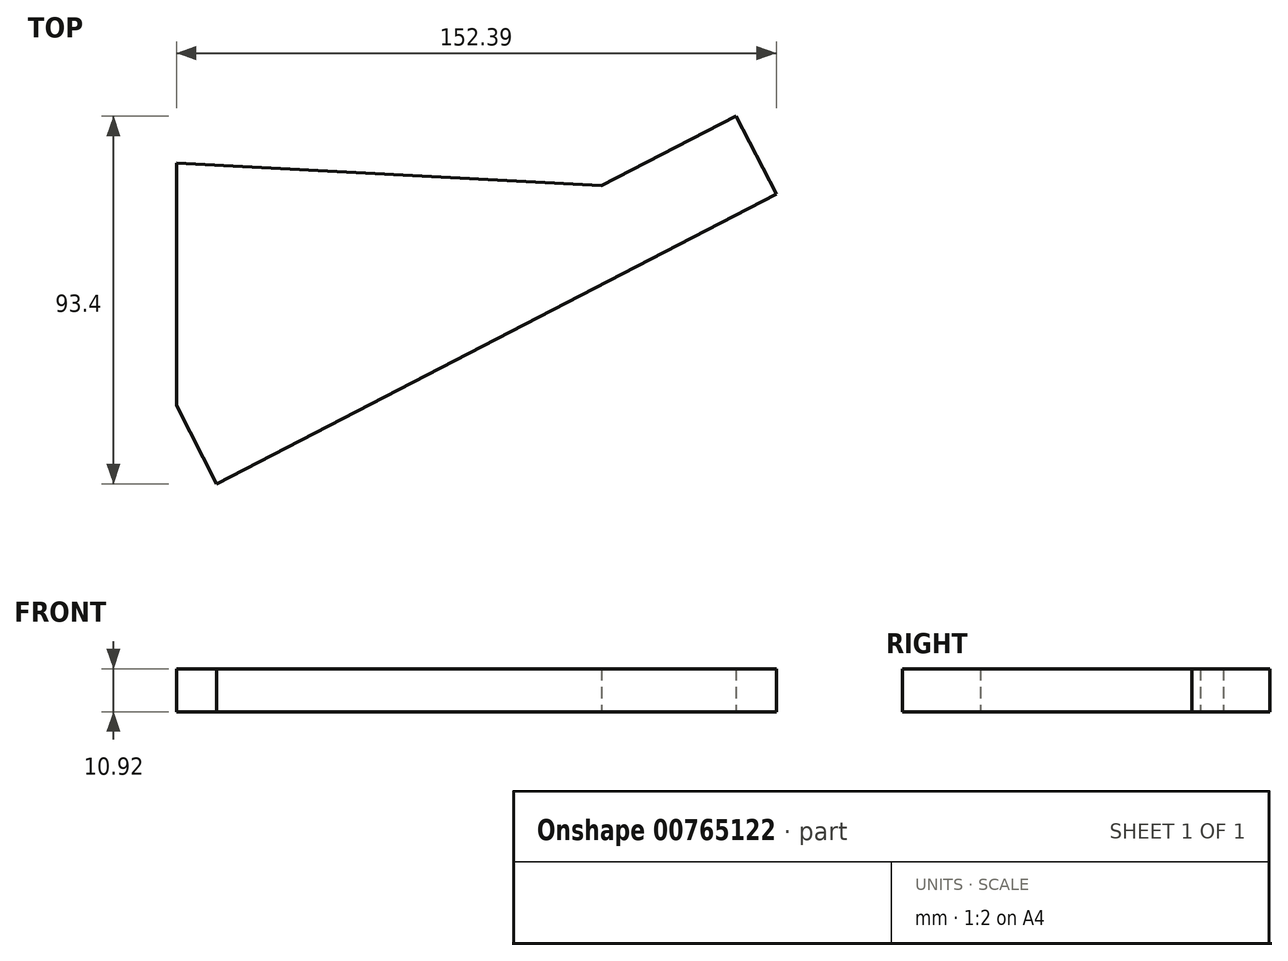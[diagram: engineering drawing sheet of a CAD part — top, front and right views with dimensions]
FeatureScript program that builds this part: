
annotation { "Feature Type Name" : "Feature", "Feature Type Description" : "" }
export const myFeature = defineFeature(function(context is Context, id is Id, definition is map)
    precondition{}
    {
        {
            var Q0;
            Q0=qCreatedBy(makeId("Top.planeOp"),FACE);
            var sketch = newSketch(context, id + "F0", { "sketchPlane" : qUnion([Q0])});
            skLineSegment(sketch, "E0", {"start": v(-132.1, -10.75) * mm, "end": v(-132.1, 51.44) * mm});
            skLineSegment(sketch, "E1", {"start": v(-132.1, 51.44) * mm, "end": v(-24.05, 45.67) * mm});
            skLineSegment(sketch, "E2", {"start": v(-24.05, 45.67) * mm, "end": v(-132.1, -10.25) * mm});
            skSolve(sketch);
        }
        {
            var Q0;
            Q0 = qSketchRegion(id + "F0", true);
            var Q1;
            {var subQ0=sQuery(id+"F0.wireOp",EDGE,"E1");Q1=makeQuery(id+"F0.imprint","IMPRINT",FACE,{"disambiguationData":[TD([[makeQuery(id+"F0.imprint","IMPRINT",EDGE,{"derivedFrom":subQ0}),-1.0]])]});}
            extrude(context, id + "F1", {"entities" : qUnion([Q0, Q1]), "depth" : 10.92 * mm, "offsetDistance" : 25.4 * mm});
        }
        {
            var Q0;
            Q0=makeQuery(id+"F1.opExtrude","SWEPT_FACE",FACE,{"disambiguationData":[OSD([sQuery(id+"F0.wireOp",EDGE,"E2")])]});
            extrude(context, id + "F2", {"entities" : qUnion([Q0]), "operationType" : NewBodyOperationType.ADD, "depth" : 22.35 * mm, "offsetDistance" : 25.4 * mm});
        }
        {
            var Q0;
            Q0=makeQuery(id+"F2.opExtrude","SWEPT_FACE",FACE,{"disambiguationData":[OSD([sQuery(id+"F0.wireOp",EDGE,"E1"),sQuery(id+"F0.wireOp",EDGE,"E2")])]});
            extrude(context, id + "F3", {"entities" : qUnion([Q0]), "operationType" : NewBodyOperationType.ADD, "depth" : 38.35 * mm, "offsetDistance" : 25.4 * mm});
        }
    });
